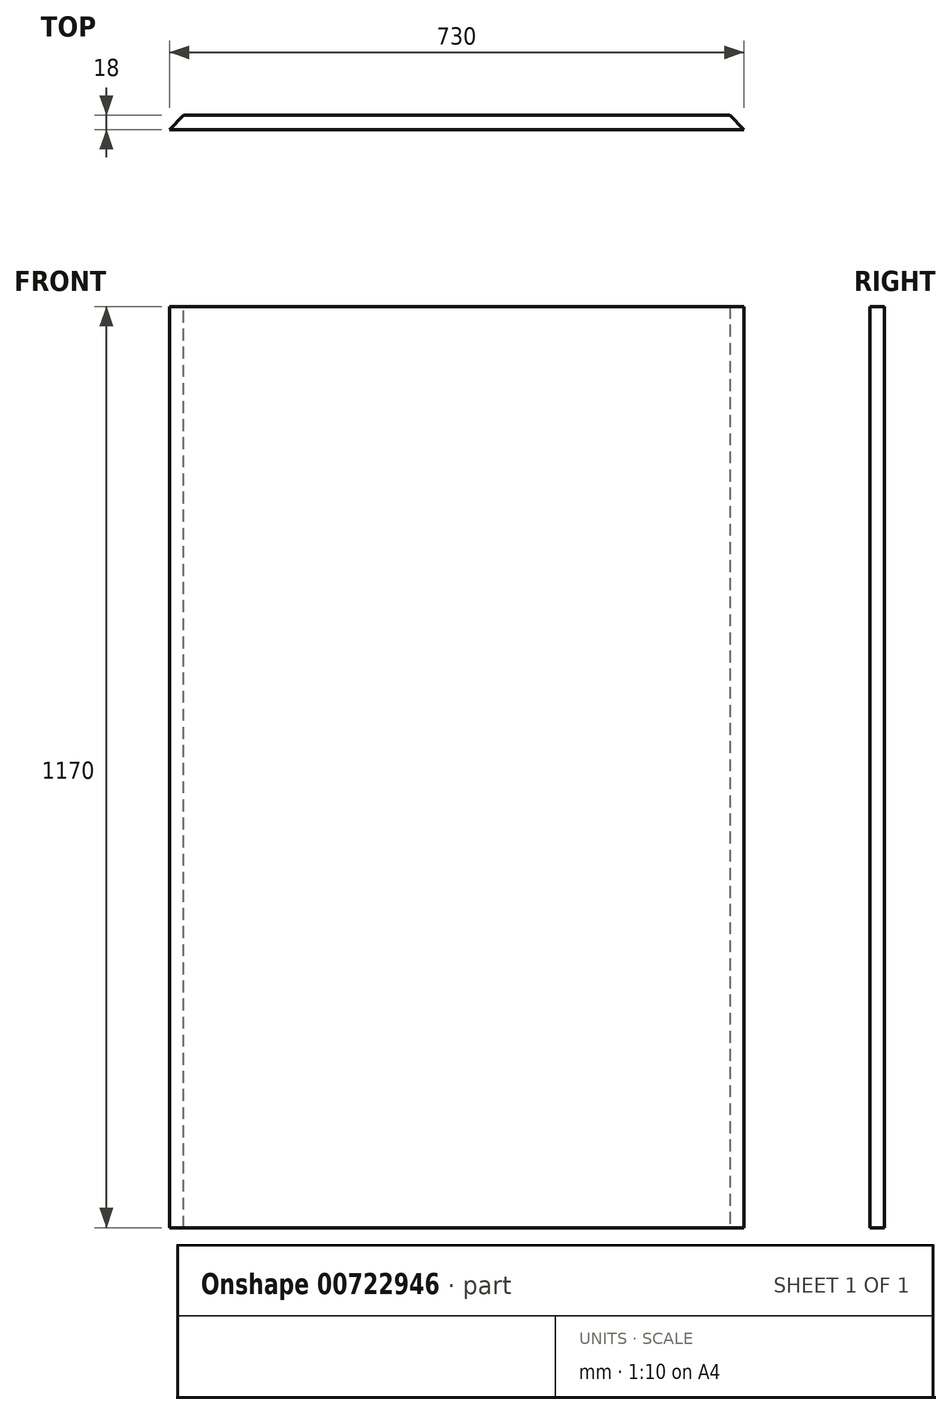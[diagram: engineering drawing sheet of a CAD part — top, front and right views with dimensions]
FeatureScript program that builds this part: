
annotation { "Feature Type Name" : "Feature", "Feature Type Description" : "" }
export const myFeature = defineFeature(function(context is Context, id is Id, definition is map)
    precondition{}
    {
        {
            var Q0;
            Q0=qCreatedBy(makeId("Front.planeOp"),FACE);
            var sketch = newSketch(context, id + "F0", { "sketchPlane" : qUnion([Q0])});
            skLineSegment(sketch, "E0.bottom", {"start": v(-365, 585) * mm, "end": v(365, 585) * mm});
            skLineSegment(sketch, "E0.top", {"start": v(-365, -585) * mm, "end": v(365, -585) * mm});
            skLineSegment(sketch, "E0.left", {"start": v(-365, 585) * mm, "end": v(-365, -585) * mm});
            skLineSegment(sketch, "E0.right", {"start": v(365, 585) * mm, "end": v(365, -585) * mm});
            skLineSegment(sketch, "E1", {"start": v(-365, 585) * mm, "end": v(365, -585) * mm, "construction": true});
            skLineSegment(sketch, "E2", {"start": v(365, 585) * mm, "end": v(-365, -585) * mm, "construction": true});
            skSolve(sketch);
        }
        {
            var Q0;
            Q0 = qSketchRegion(id + "F0", true);
            extrude(context, id + "F1", {"entities" : qUnion([Q0]), "depth" : 18 * mm, "offsetDistance" : 25 * mm});
        }
        {
            var Q0;
            Q0=makeQuery(id+"F1.opExtrude","CAP_EDGE",EDGE,{"disambiguationData":[OSD([sQuery(id+"F0.wireOp",EDGE,"E0.right")])],"isStart":true});
            var Q1;
            Q1=makeQuery(id+"F1.opExtrude","CAP_EDGE",EDGE,{"disambiguationData":[OSD([sQuery(id+"F0.wireOp",EDGE,"E0.left")])],"isStart":true});
            chamfer(context, id + "F2", {"entities" : qUnion([Q0, Q1]), "width" : 18 * mm, "tangentPropagation" : true});
        }
    });
